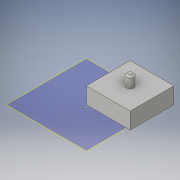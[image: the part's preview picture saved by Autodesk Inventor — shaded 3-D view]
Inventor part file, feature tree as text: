
AUTODESK INVENTOR PART (.ipt)
format: ipt  version: 2016 (Build 200138000, 138)  size: 165,888 bytes
history: native  units: mm
features: sketch x6, extrude x5, chamfer x1, plane x1, fillet x1
ambient origin geometry x8: Origin, YZ Plane, XZ Plane, XY Plane, X Axis, Y Axis, Z Axis, Center Point
bodies: Volumenkörper1 (feature_tree)
feature tree (14):
  extrude  "Extrusion1"  Depth=12.0mm
  extrude  "Extrusion2"  Depth=6.0mm
  chamfer  "Fase1"  Distance=3.0mm
  extrude  "Extrusion3"  Depth=2.0mm
  sketch  "Skizze4"  dims[d6=2.0mm d7=3.0mm d8=0.0mm]
  plane  "Arbeitsebene1"
  extrude  "Extrusion5"  Depth=2.0mm
  extrude  "Extrusion6"  Depth=2.7mm TaperAngle=0.0deg
  fillet  "Rundung1"  [1 undecoded]
  sketch  "Skizze1"  dims[d0=12.0mm d1=12.0mm]
  sketch  "Skizze2"  dims[d2=5.0mm d3=0.0mm d4=6.0mm]
  sketch  "Skizze3"  dims[d5=6.0mm]
  sketch  "Skizze5"  dims[d9=0.5mm d10=2.0mm d11=45.0deg d12=4.5mm]
  sketch  "Skizze6"  dims[d13=4.0mm d14=0.0mm d18=7.1mm d19=2.7mm d20=0.0mm d24=0.0mm d25=0.0mm d26=0.0mm d27=0.0mm d28=20.0mm d29=0.0mm d30=2.0mm]
note: 1 required parameter value undecoded (feature->parameter linkage not recoverable at this tier; creation-order binding heuristic only, values carry confidence <= 0.55)
